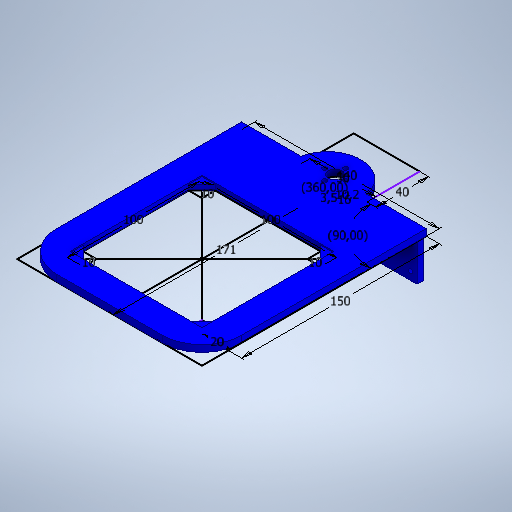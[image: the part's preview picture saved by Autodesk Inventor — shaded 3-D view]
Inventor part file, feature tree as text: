
AUTODESK INVENTOR PART (.ipt)
format: ipt  version: 2025.2 (Build 292293000, 293)  size: 349,696 bytes
history: native  units: mm
features: sketch x4, extrude x4, fillet x2, hole x1
ambient origin geometry x8: Origin, YZ Plane, XZ Plane, XY Plane, X Axis, Y Axis, Z Axis, Center Point
bodies: Body1 (feature_tree)
feature tree (11):
  sketch  "Sketch1"  dims[d0=100.0mm d1=100.0mm]
  extrude  "Extrusion3"  Depth=100.0mm
  extrude  "Extrusion4"  Depth=10.0mm
  fillet  "Fillet1"  Radius=10.0mm
  fillet  "Fillet2"  Radius=20.0mm
  extrude  "Extrusion5"  Depth=140.0mm
  hole  "Hole2"  [1 undecoded]
  extrude  "Extrusion6"  Depth=16.0mm
  sketch  "Sketch2"  dims[d36=150.0mm d37=140.0mm]
  sketch  "Sketch3"  dims[d38=90.0deg d39=50.0mm d40=40.0mm d41=5.0mm d42=0.0mm d43=4.1mm d44=0.0mm d46=30.0mm d47=25.5mm d48=136.0mm d49=34.0mm d50=5.0mm d51=34.0mm d52=5.0mm d53=30.0mm d54=0.0mm d55=5.0mm d56=6.0mm d57=5.0mm d58=6.0mm d59=24.0mm d60=18.0mm d61=24.0mm d62=18.0mm d63=3.4mm d64=6.0mm d65=4.0mm d66=2.0mm d67=90.0deg d68=8.0mm d69=20.594885mm d70=171.0mm d71=10.2mm d72=16.0mm d73=3.5mm d74=40.0mm d76=360.0deg d78=0.0mm d79=0.0mm]
  sketch  "Sketch Circular Pattern1"  dims[d14=10.0mm d15=10.0mm d16=10.0mm d35=20.0mm]
note: 1 required parameter value undecoded (feature->parameter linkage not recoverable at this tier; creation-order binding heuristic only, values carry confidence <= 0.55)
